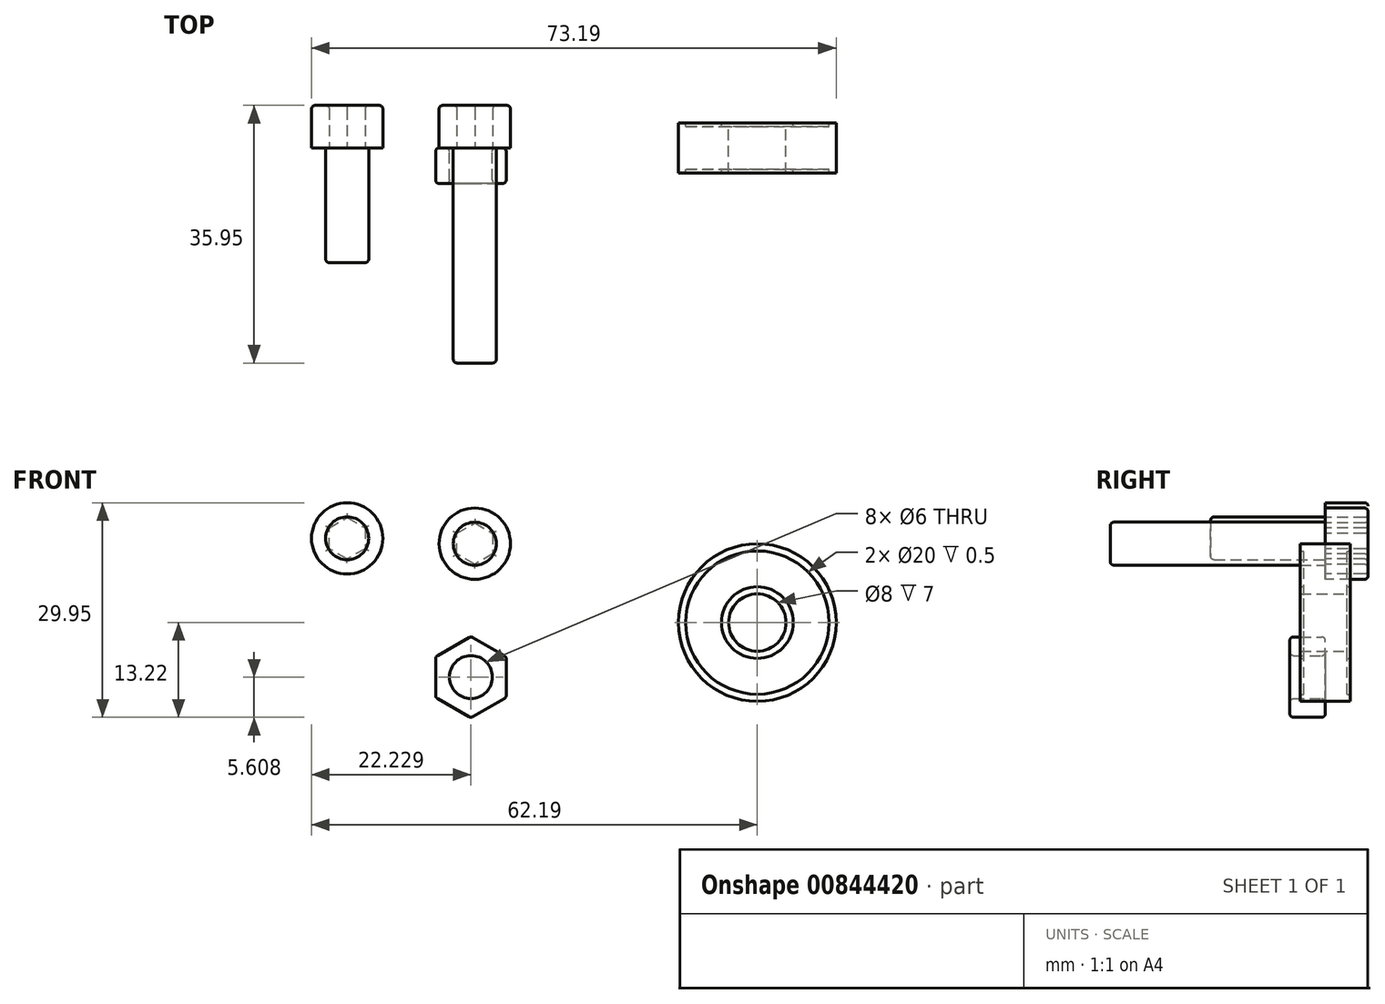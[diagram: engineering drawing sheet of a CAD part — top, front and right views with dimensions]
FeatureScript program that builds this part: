
annotation { "Feature Type Name" : "Feature", "Feature Type Description" : "" }
export const myFeature = defineFeature(function(context is Context, id is Id, definition is map)
    precondition{}
    {
        {
            var Q0;
            Q0=qCreatedBy(makeId("Front.planeOp"),FACE);
            var sketch = newSketch(context, id + "F0", { "sketchPlane" : qUnion([Q0])});
            skCircle(sketch, "E0", {"center": v(0, 0) * mm, "radius": 4 * mm});
            skCircle(sketch, "E1", {"center": v(0, 0) * mm, "radius": 5 * mm});
            skCircle(sketch, "E2", {"center": v(0, 0) * mm, "radius": 10 * mm});
            skCircle(sketch, "E3", {"center": v(0, 0) * mm, "radius": 11 * mm});
            skSolve(sketch);
        }
        {
            var Q0;
            Q0=makeQuery(id+"F0.imprint","IMPRINT",FACE,{"disambiguationData":[TD([[makeQuery(id+"F0.imprint","IMPRINT",EDGE,{"derivedFrom":sQuery(id+"F0.wireOp",EDGE,"E1")}),-1.0]])]});
            extrude(context, id + "F1", {"entities" : qUnion([Q0]), "depth" : 6 * mm, "offsetDistance" : 25 * mm, "symmetric" : true});
        }
        {
            var Q0;
            Q0=makeQuery(id+"F0.imprint","IMPRINT",FACE,{"disambiguationData":[TD([[makeQuery(id+"F0.imprint","IMPRINT",EDGE,{"derivedFrom":sQuery(id+"F0.wireOp",EDGE,"E0")}),-1.0]])]});
            var Q1;
            Q1=makeQuery(id+"F0.imprint","IMPRINT",FACE,{"disambiguationData":[TD([[makeQuery(id+"F0.imprint","IMPRINT",EDGE,{"derivedFrom":sQuery(id+"F0.wireOp",EDGE,"E2")}),-1.0]])]});
            extrude(context, id + "F2", {"entities" : qUnion([Q0, Q1]), "operationType" : NewBodyOperationType.ADD, "depth" : 7 * mm, "offsetDistance" : 25 * mm, "symmetric" : true});
        }
        {
            var Q0;
            Q0=qCreatedBy(makeId("Front.planeOp"),FACE);
            var sketch = newSketch(context, id + "F3", { "sketchPlane" : qUnion([Q0])});
            skPoint(sketch, "E4.2", {"position": v(-39.42, 11.01) * mm});
            skCircle(sketch, "E5", {"center": v(-39.42, 11.01) * mm, "radius": 3 * mm});
            skCircle(sketch, "E6", {"center": v(-39.42, 11.01) * mm, "radius": 4.97 * mm});
            skCircle(sketch, "E7.cCircle", {"center": v(-39.42, 11.01) * mm, "radius": 2.5 * mm, "construction": true});
            skLineSegment(sketch, "E7.0", {"start": v(-36.92, 12.45) * mm, "end": v(-36.92, 9.57) * mm});
            skLineSegment(sketch, "E7.1", {"start": v(-36.92, 9.57) * mm, "end": v(-39.42, 8.12) * mm});
            skLineSegment(sketch, "E7.2", {"start": v(-39.42, 8.12) * mm, "end": v(-41.92, 9.57) * mm});
            skLineSegment(sketch, "E7.3", {"start": v(-41.92, 9.57) * mm, "end": v(-41.92, 12.45) * mm});
            skLineSegment(sketch, "E7.4", {"start": v(-41.92, 12.45) * mm, "end": v(-39.42, 13.9) * mm});
            skLineSegment(sketch, "E7.5", {"start": v(-39.42, 13.9) * mm, "end": v(-36.92, 12.45) * mm});
            skPoint(sketch, "E7.0.midPoint", {"position": v(-36.92, 11.01) * mm});
            skCircle(sketch, "E8.cCircle", {"center": v(-39.96, -7.61) * mm, "radius": 4.92 * mm, "construction": true});
            skLineSegment(sketch, "E8.0", {"start": v(-39.96, -13.3) * mm, "end": v(-44.89, -10.46) * mm});
            skLineSegment(sketch, "E8.1", {"start": v(-44.89, -10.46) * mm, "end": v(-44.89, -4.77) * mm});
            skLineSegment(sketch, "E8.2", {"start": v(-44.89, -4.77) * mm, "end": v(-39.96, -1.93) * mm});
            skLineSegment(sketch, "E8.3", {"start": v(-39.96, -1.93) * mm, "end": v(-35.04, -4.77) * mm});
            skLineSegment(sketch, "E8.4", {"start": v(-35.04, -4.77) * mm, "end": v(-35.04, -10.46) * mm});
            skLineSegment(sketch, "E8.5", {"start": v(-35.04, -10.46) * mm, "end": v(-39.96, -13.3) * mm});
            skPoint(sketch, "E8.0.midPoint", {"position": v(-42.42, -11.88) * mm});
            skCircle(sketch, "E9", {"center": v(-39.96, -7.61) * mm, "radius": 3 * mm});
            skPoint(sketch, "E10.2", {"position": v(-57.22, 11.75) * mm});
            skCircle(sketch, "E11", {"center": v(-57.22, 11.75) * mm, "radius": 3 * mm});
            skCircle(sketch, "E12", {"center": v(-57.22, 11.75) * mm, "radius": 4.97 * mm});
            skCircle(sketch, "E13.cCircle", {"center": v(-57.22, 11.75) * mm, "radius": 2.5 * mm, "construction": true});
            skLineSegment(sketch, "E13.0", {"start": v(-54.72, 13.2) * mm, "end": v(-54.72, 10.31) * mm});
            skLineSegment(sketch, "E13.1", {"start": v(-54.72, 10.31) * mm, "end": v(-57.22, 8.87) * mm});
            skLineSegment(sketch, "E13.2", {"start": v(-57.22, 8.87) * mm, "end": v(-59.72, 10.31) * mm});
            skLineSegment(sketch, "E13.3", {"start": v(-59.72, 10.31) * mm, "end": v(-59.72, 13.2) * mm});
            skLineSegment(sketch, "E13.4", {"start": v(-59.72, 13.2) * mm, "end": v(-57.22, 14.64) * mm});
            skLineSegment(sketch, "E13.5", {"start": v(-57.22, 14.64) * mm, "end": v(-54.72, 13.2) * mm});
            skPoint(sketch, "E13.0.midPoint", {"position": v(-54.72, 11.75) * mm});
            skPoint(sketch, "E14", {"position": v(-41.92, 11.01) * mm});
            skSolve(sketch);
        }
        {
            var Q0;
            Q0=makeQuery(id+"F3.imprint","IMPRINT",FACE,{"disambiguationData":[TD([[makeQuery(id+"F3.imprint","IMPRINT",EDGE,{"derivedFrom":sQuery(id+"F3.wireOp",EDGE,"E11")}),1.0]])]});
            var Q1;
            Q1=makeQuery(id+"F3.imprint","IMPRINT",FACE,{"disambiguationData":[TD([[makeQuery(id+"F3.imprint","IMPRINT",EDGE,{"derivedFrom":sQuery(id+"F3.wireOp",EDGE,"E11")}),-1.0]])]});
            var Q2;
            Q2=makeQuery(id+"F3.imprint","IMPRINT",FACE,{"disambiguationData":[TD([[makeQuery(id+"F3.imprint","IMPRINT",EDGE,{"derivedFrom":sQuery(id+"F3.wireOp",EDGE,"E5")}),1.0]])]});
            var Q3;
            Q3=makeQuery(id+"F3.imprint","IMPRINT",FACE,{"disambiguationData":[TD([[makeQuery(id+"F3.imprint","IMPRINT",EDGE,{"derivedFrom":sQuery(id+"F3.wireOp",EDGE,"E5")}),-1.0]])]});
            extrude(context, id + "F4", {"entities" : qUnion([Q0, Q1, Q2, Q3]), "oppositeDirection" : true, "depth" : 5.95 * mm, "offsetDistance" : 25 * mm});
        }
        {
            var Q0;
            Q0=makeQuery(id+"F3.imprint","IMPRINT",FACE,{"disambiguationData":[TD([[makeQuery(id+"F3.imprint","IMPRINT",EDGE,{"derivedFrom":sQuery(id+"F3.wireOp",EDGE,"E7.0")}),-1.0]])]});
            var Q1;
            Q1=makeQuery(id+"F3.imprint","IMPRINT",FACE,{"disambiguationData":[TD([[makeQuery(id+"F3.imprint","IMPRINT",EDGE,{"derivedFrom":sQuery(id+"F3.wireOp",EDGE,"E5")}),1.0]])]});
            extrude(context, id + "F5", {"entities" : qUnion([Q0, Q1]), "operationType" : NewBodyOperationType.ADD, "depth" : 30 * mm, "offsetDistance" : 25 * mm});
        }
        {
            var Q0;
            Q0=makeQuery(id+"F3.imprint","IMPRINT",FACE,{"disambiguationData":[TD([[makeQuery(id+"F3.imprint","IMPRINT",EDGE,{"derivedFrom":sQuery(id+"F3.wireOp",EDGE,"E11")}),1.0]])]});
            var Q1;
            Q1=makeQuery(id+"F3.imprint","IMPRINT",FACE,{"disambiguationData":[TD([[makeQuery(id+"F3.imprint","IMPRINT",EDGE,{"derivedFrom":sQuery(id+"F3.wireOp",EDGE,"E13.0")}),-1.0]])]});
            extrude(context, id + "F6", {"entities" : qUnion([Q0, Q1]), "operationType" : NewBodyOperationType.ADD, "depth" : 16 * mm, "offsetDistance" : 25 * mm});
        }
        {
            var Q0;
            Q0=makeQuery(id+"F3.imprint","IMPRINT",FACE,{"disambiguationData":[TD([[makeQuery(id+"F3.imprint","IMPRINT",EDGE,{"derivedFrom":sQuery(id+"F3.wireOp",EDGE,"E8.0")}),-1.0]])]});
            extrude(context, id + "F7", {"entities" : qUnion([Q0]), "depth" : 4.95 * mm, "offsetDistance" : 25 * mm});
        }
        {
            var Q0;
            Q0=makeQuery(id+"F4.opExtrude","CAP_FACE",FACE,{"disambiguationData":[OSD([sQuery(id+"F3.wireOp",EDGE,"E6"),sQuery(id+"F3.wireOp",EDGE,"E7.0"),sQuery(id+"F3.wireOp",EDGE,"E7.1"),sQuery(id+"F3.wireOp",EDGE,"E7.2"),sQuery(id+"F3.wireOp",EDGE,"E7.3"),sQuery(id+"F3.wireOp",EDGE,"E7.4"),sQuery(id+"F3.wireOp",EDGE,"E7.5")])],"isStart":false});
            var Q1;
            Q1=makeQuery(id+"F7.opExtrude","CAP_FACE",FACE,{"disambiguationData":[OSD([sQuery(id+"F3.wireOp",EDGE,"E8.0"),sQuery(id+"F3.wireOp",EDGE,"E8.1"),sQuery(id+"F3.wireOp",EDGE,"E8.2"),sQuery(id+"F3.wireOp",EDGE,"E8.3"),sQuery(id+"F3.wireOp",EDGE,"E8.4"),sQuery(id+"F3.wireOp",EDGE,"E8.5"),sQuery(id+"F3.wireOp",EDGE,"E9")])],"isStart":true});
            var Q2;
            Q2=makeQuery(id+"F7.opExtrude","CAP_FACE",FACE,{"disambiguationData":[OSD([sQuery(id+"F3.wireOp",EDGE,"E8.0"),sQuery(id+"F3.wireOp",EDGE,"E8.1"),sQuery(id+"F3.wireOp",EDGE,"E8.2"),sQuery(id+"F3.wireOp",EDGE,"E8.3"),sQuery(id+"F3.wireOp",EDGE,"E8.4"),sQuery(id+"F3.wireOp",EDGE,"E8.5"),sQuery(id+"F3.wireOp",EDGE,"E9")])],"isStart":false});
            var Q3;
            Q3=makeQuery(id+"F7.opExtrude","SWEPT_EDGE",EDGE,{"disambiguationData":[OSD([sQuery(id+"F3.wireOp",EDGE,"E8.2"),sQuery(id+"F3.wireOp",EDGE,"E8.3")])]});
            var Q4;
            Q4=makeQuery(id+"F7.opExtrude","SWEPT_EDGE",EDGE,{"disambiguationData":[OSD([sQuery(id+"F3.wireOp",EDGE,"E8.3"),sQuery(id+"F3.wireOp",EDGE,"E8.4")])]});
            var Q5;
            Q5=makeQuery(id+"F7.opExtrude","SWEPT_EDGE",EDGE,{"disambiguationData":[OSD([sQuery(id+"F3.wireOp",EDGE,"E8.1"),sQuery(id+"F3.wireOp",EDGE,"E8.2")])]});
            var Q6;
            Q6=makeQuery(id+"F7.opExtrude","SWEPT_EDGE",EDGE,{"disambiguationData":[OSD([sQuery(id+"F3.wireOp",EDGE,"E8.0"),sQuery(id+"F3.wireOp",EDGE,"E8.1")])]});
            var Q7;
            Q7=makeQuery(id+"F7.opExtrude","SWEPT_EDGE",EDGE,{"disambiguationData":[OSD([sQuery(id+"F3.wireOp",EDGE,"E8.0"),sQuery(id+"F3.wireOp",EDGE,"E8.5")])]});
            var Q8;
            Q8=makeQuery(id+"F7.opExtrude","SWEPT_EDGE",EDGE,{"disambiguationData":[OSD([sQuery(id+"F3.wireOp",EDGE,"E8.4"),sQuery(id+"F3.wireOp",EDGE,"E8.5")])]});
            var Q9;
            Q9=makeQuery(id+"F5.opExtrude","CAP_FACE",FACE,{"disambiguationData":[OSD([sQuery(id+"F3.wireOp",EDGE,"E5")])],"isStart":false});
            var Q10;
            Q10=makeQuery(id+"F6.opExtrude","CAP_FACE",FACE,{"disambiguationData":[OSD([sQuery(id+"F3.wireOp",EDGE,"E11")])],"isStart":false});
            var Q11;
            Q11=makeQuery(id+"F4.opExtrude","CAP_FACE",FACE,{"disambiguationData":[OSD([sQuery(id+"F3.wireOp",EDGE,"E12"),sQuery(id+"F3.wireOp",EDGE,"E13.0"),sQuery(id+"F3.wireOp",EDGE,"E13.1"),sQuery(id+"F3.wireOp",EDGE,"E13.2"),sQuery(id+"F3.wireOp",EDGE,"E13.3"),sQuery(id+"F3.wireOp",EDGE,"E13.4"),sQuery(id+"F3.wireOp",EDGE,"E13.5")])],"isStart":false});
            fillet(context, id + "F8", {"entities" : qUnion([Q0, Q1, Q2, Q3, Q4, Q5, Q6, Q7, Q8, Q9, Q10, Q11]), "radius" : 0.5 * mm, "tangentPropagation" : true, "allowEdgeOverflow" : false});
        }
    });
